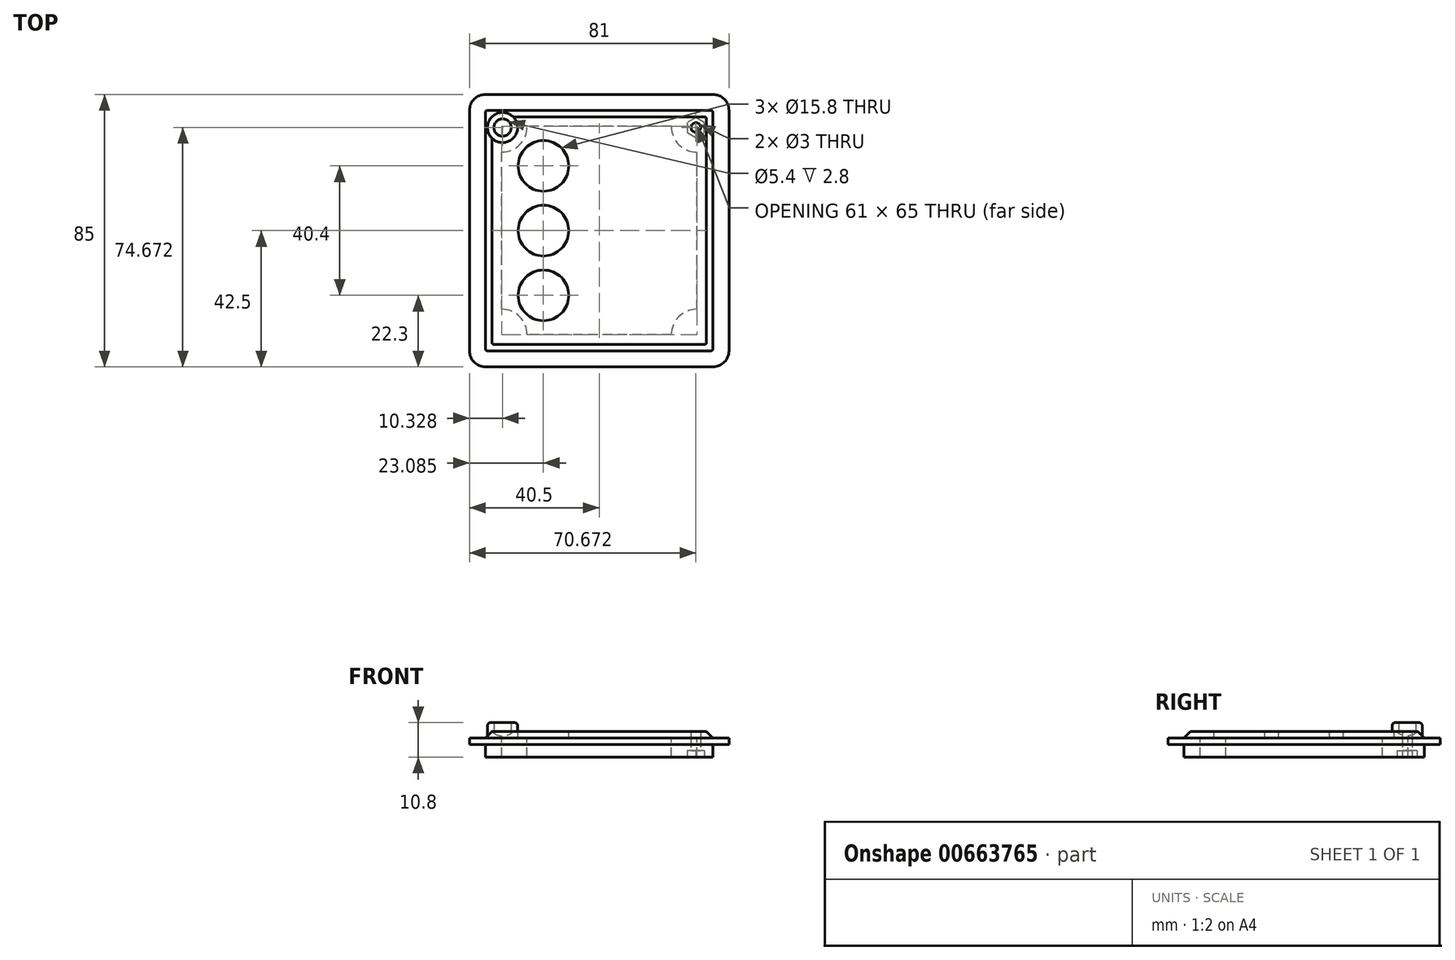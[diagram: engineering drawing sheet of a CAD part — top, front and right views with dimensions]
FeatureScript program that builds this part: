
annotation { "Feature Type Name" : "Feature", "Feature Type Description" : "" }
export const myFeature = defineFeature(function(context is Context, id is Id, definition is map)
    precondition{}
    {
        {
            var Q0;
            Q0=qCreatedBy(makeId("Top.planeOp"),FACE);
            var sketch = newSketch(context, id + "F0", { "sketchPlane" : qUnion([Q0])});
            skLineSegment(sketch, "E0.bottom", {"start": v(35.5, -37.5) * mm, "end": v(-35.5, -37.5) * mm});
            skLineSegment(sketch, "E0.top", {"start": v(35.5, 37.5) * mm, "end": v(-35.5, 37.5) * mm});
            skLineSegment(sketch, "E0.left", {"start": v(35.5, -37.5) * mm, "end": v(35.5, 37.5) * mm});
            skLineSegment(sketch, "E0.right", {"start": v(-35.5, -37.5) * mm, "end": v(-35.5, 37.5) * mm});
            skPoint(sketch, "E0.middle", {"position": v(0, 0) * mm});
            skSolve(sketch);
        }
        {
            var Q0;
            Q0=qSketchRegion(id+"F0",true);
            extrude(context, id + "F1", {"entities" : qUnion([Q0]), "depth" : 4 * mm, "offsetDistance" : 25 * mm});
        }
        {
            var Q0;
            Q0=makeQuery(id+"F1.opExtrude","CAP_FACE",FACE,{"disambiguationData":[OSD([sQuery(id+"F0.wireOp",EDGE,"E0.bottom"),sQuery(id+"F0.wireOp",EDGE,"E0.top"),sQuery(id+"F0.wireOp",EDGE,"E0.left"),sQuery(id+"F0.wireOp",EDGE,"E0.right")])],"isStart":false});
            var sketch = newSketch(context, id + "F2", { "sketchPlane" : qUnion([Q0])});
            skLineSegment(sketch, "E1.bottom", {"start": v(30.5, -32.5) * mm, "end": v(22.5, -32.5) * mm, "construction": true});
            skLineSegment(sketch, "E1.top", {"start": v(30.5, 32.5) * mm, "end": v(22.5, 32.5) * mm, "construction": true});
            skLineSegment(sketch, "E1.left", {"start": v(30.5, -32.5) * mm, "end": v(30.5, -24.5) * mm, "construction": true});
            skLineSegment(sketch, "E1.right", {"start": v(-30.5, -32.5) * mm, "end": v(-30.5, -24.5) * mm, "construction": true});
            skPoint(sketch, "E1.middle", {"position": v(0, 0) * mm});
            skArc(sketch, "E2", {"start": v(-30.5, 24.5) * mm, "mid": v(-24.84, 26.84) * mm, "end": v(-22.5, 32.5) * mm});
            skLineSegment(sketch, "E3", {"start": v(-22.5, 32.5) * mm, "end": v(-30.5, 32.5) * mm, "construction": true});
            skLineSegment(sketch, "E4", {"start": v(-30.5, 24.5) * mm, "end": v(-30.5, 32.5) * mm, "construction": true});
            skArc(sketch, "E5.MirrorCS", {"start": v(30.5, 24.5) * mm, "mid": v(24.84, 26.84) * mm, "end": v(22.5, 32.5) * mm});
            skArc(sketch, "E6.MirrorCS", {"start": v(-30.5, -24.5) * mm, "mid": v(-24.84, -26.84) * mm, "end": v(-22.5, -32.5) * mm});
            skArc(sketch, "E7.MirrorCS", {"start": v(30.5, -24.5) * mm, "mid": v(24.84, -26.84) * mm, "end": v(22.5, -32.5) * mm});
            skLineSegment(sketch, "E8", {"start": v(-30.5, -24.5) * mm, "end": v(-30.5, 24.5) * mm});
            skLineSegment(sketch, "E9", {"start": v(-22.5, -32.5) * mm, "end": v(-30.5, -32.5) * mm, "construction": true});
            skLineSegment(sketch, "E10", {"start": v(22.5, -32.5) * mm, "end": v(-22.5, -32.5) * mm});
            skLineSegment(sketch, "E11", {"start": v(30.5, -24.5) * mm, "end": v(30.5, 24.5) * mm});
            skLineSegment(sketch, "E12", {"start": v(30.5, 24.5) * mm, "end": v(30.5, 32.5) * mm, "construction": true});
            skLineSegment(sketch, "E13", {"start": v(22.5, 32.5) * mm, "end": v(-22.5, 32.5) * mm});
            skSolve(sketch);
        }
        {
            var Q0;
            Q0=makeQuery(id+"F2.imprint","IMPRINT",FACE,{"disambiguationData":[TD([[makeQuery(id+"F2.imprint","IMPRINT",EDGE,{"derivedFrom":sQuery(id+"F2.wireOp",EDGE,"E2")}),-1.0]])]});
            extrude(context, id + "F3", {"entities" : qUnion([Q0]), "operationType" : NewBodyOperationType.REMOVE, "oppositeDirection" : true, "depth" : 25 * mm, "offsetDistance" : 25 * mm});
        }
        {
            var Q0;
            Q0=makeQuery(id+"F1.opExtrude","CAP_FACE",FACE,{"disambiguationData":[OSD([sQuery(id+"F0.wireOp",EDGE,"E0.bottom"),sQuery(id+"F0.wireOp",EDGE,"E0.top"),sQuery(id+"F0.wireOp",EDGE,"E0.left"),sQuery(id+"F0.wireOp",EDGE,"E0.right")])],"isStart":false});
            var sketch = newSketch(context, id + "F4", { "sketchPlane" : qUnion([Q0])});
            skLineSegment(sketch, "E14.bottom", {"start": v(35.5, -42.5) * mm, "end": v(-35.5, -42.5) * mm});
            skLineSegment(sketch, "E14.top", {"start": v(35.5, 42.5) * mm, "end": v(-35.5, 42.5) * mm});
            skLineSegment(sketch, "E14.left", {"start": v(40.5, -37.5) * mm, "end": v(40.5, 37.5) * mm});
            skLineSegment(sketch, "E14.right", {"start": v(-40.5, -37.5) * mm, "end": v(-40.5, 37.5) * mm});
            skPoint(sketch, "E14.middle", {"position": v(0, 0) * mm});
            skPoint(sketch, "E15.visualSharp", {"position": v(-40.5, 42.5) * mm});
            skArc(sketch, "E15.filletArc", {"start": v(-35.5, 42.5) * mm, "mid": v(-39.04, 41.04) * mm, "end": v(-40.5, 37.5) * mm});
            skPoint(sketch, "E16.visualSharp", {"position": v(40.5, 42.5) * mm});
            skArc(sketch, "E16.filletArc", {"start": v(40.5, 37.5) * mm, "mid": v(39.04, 41.04) * mm, "end": v(35.5, 42.5) * mm});
            skPoint(sketch, "E17.visualSharp", {"position": v(40.5, -42.5) * mm});
            skArc(sketch, "E17.filletArc", {"start": v(35.5, -42.5) * mm, "mid": v(39.04, -41.04) * mm, "end": v(40.5, -37.5) * mm});
            skPoint(sketch, "E18.visualSharp", {"position": v(-40.5, -42.5) * mm});
            skArc(sketch, "E18.filletArc", {"start": v(-40.5, -37.5) * mm, "mid": v(-39.04, -41.04) * mm, "end": v(-35.5, -42.5) * mm});
            skArc(sketch, "E19.0", {"start": v(-30.5, 24.5) * mm, "mid": v(-24.84, 26.84) * mm, "end": v(-22.5, 32.5) * mm});
            skLineSegment(sketch, "E19.1", {"start": v(22.5, 32.5) * mm, "end": v(-22.5, 32.5) * mm});
            skArc(sketch, "E19.2", {"start": v(30.5, 24.5) * mm, "mid": v(24.84, 26.84) * mm, "end": v(22.5, 32.5) * mm});
            skLineSegment(sketch, "E19.3", {"start": v(30.5, -24.5) * mm, "end": v(30.5, 24.5) * mm});
            skArc(sketch, "E19.4", {"start": v(30.5, -24.5) * mm, "mid": v(24.84, -26.84) * mm, "end": v(22.5, -32.5) * mm});
            skLineSegment(sketch, "E19.5", {"start": v(22.5, -32.5) * mm, "end": v(-22.5, -32.5) * mm});
            skArc(sketch, "E19.6", {"start": v(-30.5, -24.5) * mm, "mid": v(-24.84, -26.84) * mm, "end": v(-22.5, -32.5) * mm});
            skLineSegment(sketch, "E19.7", {"start": v(-30.5, -24.5) * mm, "end": v(-30.5, 24.5) * mm});
            skSolve(sketch);
        }
        {
            var Q0;
            Q0=qSketchRegion(id+"F4",true);
            extrude(context, id + "F5", {"entities" : qUnion([Q0]), "operationType" : NewBodyOperationType.ADD, "depth" : 2 * mm, "offsetDistance" : 25 * mm});
        }
        {
            var Q0;
            Q0=makeQuery(id+"F1.opExtrude","CAP_FACE",FACE,{"disambiguationData":[OSD([sQuery(id+"F0.wireOp",EDGE,"E0.bottom"),sQuery(id+"F0.wireOp",EDGE,"E0.top"),sQuery(id+"F0.wireOp",EDGE,"E0.left"),sQuery(id+"F0.wireOp",EDGE,"E0.right")])],"isStart":true});
            var sketch = newSketch(context, id + "F6", { "sketchPlane" : qUnion([Q0])});
            skLineSegment(sketch, "E20", {"start": v(35.5, -37.5) * mm, "end": v(24.84, -26.84) * mm, "construction": true});
            skCircle(sketch, "E21.cCircle", {"center": v(30.17, -32.17) * mm, "radius": 2.7 * mm, "construction": true});
            skLineSegment(sketch, "E21.0", {"start": v(27.47, -33.73) * mm, "end": v(27.47, -30.61) * mm});
            skLineSegment(sketch, "E21.1", {"start": v(27.47, -30.61) * mm, "end": v(30.17, -29.05) * mm});
            skLineSegment(sketch, "E21.2", {"start": v(30.17, -29.05) * mm, "end": v(32.87, -30.61) * mm});
            skLineSegment(sketch, "E21.3", {"start": v(32.87, -30.61) * mm, "end": v(32.87, -33.73) * mm});
            skLineSegment(sketch, "E21.4", {"start": v(32.87, -33.73) * mm, "end": v(30.17, -35.29) * mm});
            skLineSegment(sketch, "E21.5", {"start": v(30.17, -35.29) * mm, "end": v(27.47, -33.73) * mm});
            skPoint(sketch, "E21.0.midPoint", {"position": v(27.47, -32.17) * mm});
            skSolve(sketch);
        }
        {
            var Q0;
            Q0=qSketchRegion(id+"F6",true);
            extrude(context, id + "F7", {"entities" : qUnion([Q0]), "operationType" : NewBodyOperationType.REMOVE, "oppositeDirection" : true, "depth" : 2 * mm, "offsetDistance" : 25 * mm});
        }
        {
            var Q0;
            Q0=makeQuery(id+"F5.opExtrude","CAP_FACE",FACE,{"disambiguationData":[OSD([sQuery(id+"F4.wireOp",EDGE,"E14.bottom"),sQuery(id+"F4.wireOp",EDGE,"E14.top"),sQuery(id+"F4.wireOp",EDGE,"E14.left"),sQuery(id+"F4.wireOp",EDGE,"E14.right"),sQuery(id+"F4.wireOp",EDGE,"E15.filletArc"),sQuery(id+"F4.wireOp",EDGE,"E16.filletArc"),sQuery(id+"F4.wireOp",EDGE,"E17.filletArc"),sQuery(id+"F4.wireOp",EDGE,"E18.filletArc"),sQuery(id+"F4.wireOp",EDGE,"E19.0"),sQuery(id+"F4.wireOp",EDGE,"E19.1"),sQuery(id+"F4.wireOp",EDGE,"E19.2"),sQuery(id+"F4.wireOp",EDGE,"E19.3"),sQuery(id+"F4.wireOp",EDGE,"E19.4"),sQuery(id+"F4.wireOp",EDGE,"E19.5"),sQuery(id+"F4.wireOp",EDGE,"E19.6"),sQuery(id+"F4.wireOp",EDGE,"E19.7")])],"isStart":false});
            var sketch = newSketch(context, id + "F8", { "sketchPlane" : qUnion([Q0])});
            skLineSegment(sketch, "E22.bottom", {"start": v(-35.5, 37.5) * mm, "end": v(35.5, 37.5) * mm});
            skLineSegment(sketch, "E22.top", {"start": v(-35.5, -37.5) * mm, "end": v(35.5, -37.5) * mm});
            skLineSegment(sketch, "E22.left", {"start": v(-35.5, 37.5) * mm, "end": v(-35.5, -37.5) * mm});
            skLineSegment(sketch, "E22.right", {"start": v(35.5, 37.5) * mm, "end": v(35.5, -37.5) * mm});
            skPoint(sketch, "E22.middle", {"position": v(0, 0) * mm});
            skLineSegment(sketch, "E23", {"start": v(-30.5, 0) * mm, "end": v(-40.5, 0) * mm});
            skPoint(sketch, "E24", {"position": v(-35.5, 0) * mm});
            skLineSegment(sketch, "E25", {"start": v(0, -42.5) * mm, "end": v(0, -32.5) * mm, "construction": true});
            skPoint(sketch, "E26", {"position": v(0, -37.5) * mm});
            skSolve(sketch);
        }
        {
            var Q0;
            Q0=qSketchRegion(id+"F8",true);
            extrude(context, id + "F9", {"entities" : qUnion([Q0]), "depth" : 2 * mm, "offsetDistance" : 25 * mm});
        }
        {
            var Q0;
            Q0=makeQuery(id+"F1.opExtrude","CAP_FACE",FACE,{"disambiguationData":[OSD([sQuery(id+"F0.wireOp",EDGE,"E0.bottom"),sQuery(id+"F0.wireOp",EDGE,"E0.top"),sQuery(id+"F0.wireOp",EDGE,"E0.left"),sQuery(id+"F0.wireOp",EDGE,"E0.right")])],"isStart":true});
            var sketch = newSketch(context, id + "F10", { "sketchPlane" : qUnion([Q0])});
            skPoint(sketch, "E27.0", {"position": v(30.17, -32.17) * mm});
            skCircle(sketch, "E28", {"center": v(30.17, -32.17) * mm, "radius": 1.5 * mm});
            skSolve(sketch);
        }
        {
            var Q0;
            Q0=qSketchRegion(id+"F10",true);
            extrude(context, id + "F11", {"entities" : qUnion([Q0]), "operationType" : NewBodyOperationType.REMOVE, "oppositeDirection" : true, "depth" : 25 * mm, "offsetDistance" : 25 * mm});
        }
        {
            var Q0;
            Q0=makeQuery(id+"F9.opExtrude","CAP_FACE",FACE,{"disambiguationData":[OSD([sQuery(id+"F8.wireOp",EDGE,"E22.bottom"),sQuery(id+"F8.wireOp",EDGE,"E22.top"),sQuery(id+"F8.wireOp",EDGE,"E22.left"),sQuery(id+"F8.wireOp",EDGE,"E22.right")])],"isStart":false});
            var sketch = newSketch(context, id + "F12", { "sketchPlane" : qUnion([Q0])});
            skCircle(sketch, "E29", {"center": v(-17.41, 20.2) * mm, "radius": 7.9 * mm});
            skCircle(sketch, "E30", {"center": v(-17.41, 0) * mm, "radius": 7.9 * mm});
            skCircle(sketch, "E31", {"center": v(-17.41, -20.2) * mm, "radius": 7.9 * mm});
            skLineSegment(sketch, "E32.0", {"start": v(22.5, 32.5) * mm, "end": v(-22.5, 32.5) * mm, "construction": true});
            skLineSegment(sketch, "E32.1", {"start": v(22.5, -32.5) * mm, "end": v(-22.5, -32.5) * mm, "construction": true});
            skLineSegment(sketch, "E32.2", {"start": v(-30.5, -24.5) * mm, "end": v(-30.5, 24.5) * mm, "construction": true});
            skArc(sketch, "E32.3", {"start": v(-30.5, -24.5) * mm, "mid": v(-24.84, -26.84) * mm, "end": v(-22.5, -32.5) * mm, "construction": true});
            skArc(sketch, "E32.4", {"start": v(-30.5, 24.5) * mm, "mid": v(-24.84, 26.84) * mm, "end": v(-22.5, 32.5) * mm, "construction": true});
            skArc(sketch, "E32.5", {"start": v(30.5, 24.5) * mm, "mid": v(24.84, 26.84) * mm, "end": v(22.5, 32.5) * mm, "construction": true});
            skLineSegment(sketch, "E32.6", {"start": v(30.5, -24.5) * mm, "end": v(30.5, 24.5) * mm, "construction": true});
            skArc(sketch, "E32.7", {"start": v(30.5, -24.5) * mm, "mid": v(24.84, -26.84) * mm, "end": v(22.5, -32.5) * mm, "construction": true});
            skLineSegment(sketch, "E33", {"start": v(-17.41, 32.5) * mm, "end": v(-17.41, 7.9) * mm, "construction": true});
            skPoint(sketch, "E34", {"position": v(-6.45, 20.2) * mm});
            skPoint(sketch, "E35", {"position": v(22.5, 20.2) * mm});
            skSolve(sketch);
        }
        {
            var Q0;
            Q0=qSketchRegion(id+"F12",true);
            extrude(context, id + "F13", {"entities" : qUnion([Q0]), "operationType" : NewBodyOperationType.REMOVE, "oppositeDirection" : true, "depth" : 25 * mm, "offsetDistance" : 25 * mm});
        }
        {
            var Q0;
            Q0=makeQuery(id+"F12.imprint","IMPRINT",FACE,{"disambiguationData":[TD([[makeQuery(id+"F12.imprint","IMPRINT",EDGE,{"derivedFrom":sQuery(id+"F12.wireOp",EDGE,"E29")}),-1.0]])]});
            var sketch = newSketch(context, id + "F14", { "sketchPlane" : qUnion([Q0])});
            skCircle(sketch, "E36.0", {"center": v(-30.17, 32.17) * mm, "radius": 1.5 * mm, "construction": true});
            skCircle(sketch, "E37", {"center": v(-30.17, 32.17) * mm, "radius": 2.7 * mm});
            skCircle(sketch, "E38", {"center": v(-30.17, 32.17) * mm, "radius": 4.7 * mm});
            skSolve(sketch);
        }
        {
            var Q0;
            Q0=makeQuery(id+"F14.imprint","IMPRINT",FACE,{"disambiguationData":[TD([[makeQuery(id+"F14.imprint","IMPRINT",EDGE,{"derivedFrom":sQuery(id+"F14.wireOp",EDGE,"E37")}),-1.0]])]});
            extrude(context, id + "F15", {"entities" : qUnion([Q0]), "operationType" : NewBodyOperationType.ADD, "depth" : 2.8 * mm, "offsetDistance" : 25 * mm});
        }
        {
            var Q0;
            Q0=makeQuery(id+"F15.opExtrude","CAP_EDGE",EDGE,{"disambiguationData":[OSD([sQuery(id+"F14.wireOp",EDGE,"E38")])],"isStart":false});
            fillet(context, id + "F16", {"entities" : qUnion([Q0]), "radius" : 1 * mm, "tangentPropagation" : true, "allowEdgeOverflow" : false});
        }
        {
            var Q0;
            Q0=makeQuery(id+"F9.opExtrude","CAP_EDGE",EDGE,{"disambiguationData":[OSD([sQuery(id+"F8.wireOp",EDGE,"E22.left")])],"isStart":false});
            var Q1;
            Q1=makeQuery(id+"F9.opExtrude","CAP_EDGE",EDGE,{"disambiguationData":[OSD([sQuery(id+"F8.wireOp",EDGE,"E22.bottom")])],"isStart":false});
            var Q2;
            Q2=makeQuery(id+"F9.opExtrude","CAP_EDGE",EDGE,{"disambiguationData":[OSD([sQuery(id+"F8.wireOp",EDGE,"E22.right")])],"isStart":false});
            var Q3;
            Q3=makeQuery(id+"F9.opExtrude","CAP_EDGE",EDGE,{"disambiguationData":[OSD([sQuery(id+"F8.wireOp",EDGE,"E22.top")])],"isStart":false});
            chamfer(context, id + "F17", {"entities" : qUnion([Q0, Q1, Q2, Q3]), "width" : 2 * mm, "tangentPropagation" : true});
        }
        {
            var Q0;
            Q0=makeQuery(id+"F17.opChamfer","BLEND_EDGE",EDGE,{"blendedFrom":[makeQuery(id+"F9.opExtrude","CAP_EDGE",EDGE,{"disambiguationData":[OSD([sQuery(id+"F8.wireOp",EDGE,"E22.top")])],"isStart":false}),makeQuery(id+"F9.opExtrude","CAP_EDGE",EDGE,{"disambiguationData":[OSD([sQuery(id+"F8.wireOp",EDGE,"E22.left")])],"isStart":false})],"blendedInto":[]});
            var Q1;
            Q1=makeQuery(id+"F17.opChamfer","BLEND_EDGE",EDGE,{"blendedFrom":[makeQuery(id+"F9.opExtrude","CAP_EDGE",EDGE,{"disambiguationData":[OSD([sQuery(id+"F8.wireOp",EDGE,"E22.top")])],"isStart":false}),makeQuery(id+"F9.opExtrude","CAP_EDGE",EDGE,{"disambiguationData":[OSD([sQuery(id+"F8.wireOp",EDGE,"E22.right")])],"isStart":false})],"blendedInto":[]});
            var Q2;
            Q2=makeQuery(id+"F17.opChamfer","BLEND_EDGE",EDGE,{"blendedFrom":[makeQuery(id+"F9.opExtrude","CAP_EDGE",EDGE,{"disambiguationData":[OSD([sQuery(id+"F8.wireOp",EDGE,"E22.bottom")])],"isStart":false}),makeQuery(id+"F9.opExtrude","CAP_EDGE",EDGE,{"disambiguationData":[OSD([sQuery(id+"F8.wireOp",EDGE,"E22.left")])],"isStart":false})],"blendedInto":[]});
            var Q3;
            Q3=makeQuery(id+"F17.opChamfer","BLEND_EDGE",EDGE,{"blendedFrom":[makeQuery(id+"F9.opExtrude","CAP_EDGE",EDGE,{"disambiguationData":[OSD([sQuery(id+"F8.wireOp",EDGE,"E22.bottom")])],"isStart":false}),makeQuery(id+"F9.opExtrude","CAP_EDGE",EDGE,{"disambiguationData":[OSD([sQuery(id+"F8.wireOp",EDGE,"E22.right")])],"isStart":false})],"blendedInto":[]});
            fillet(context, id + "F18", {"entities" : qUnion([Q0, Q1, Q2, Q3]), "radius" : 1 * mm, "tangentPropagation" : true, "allowEdgeOverflow" : false});
        }
    });
